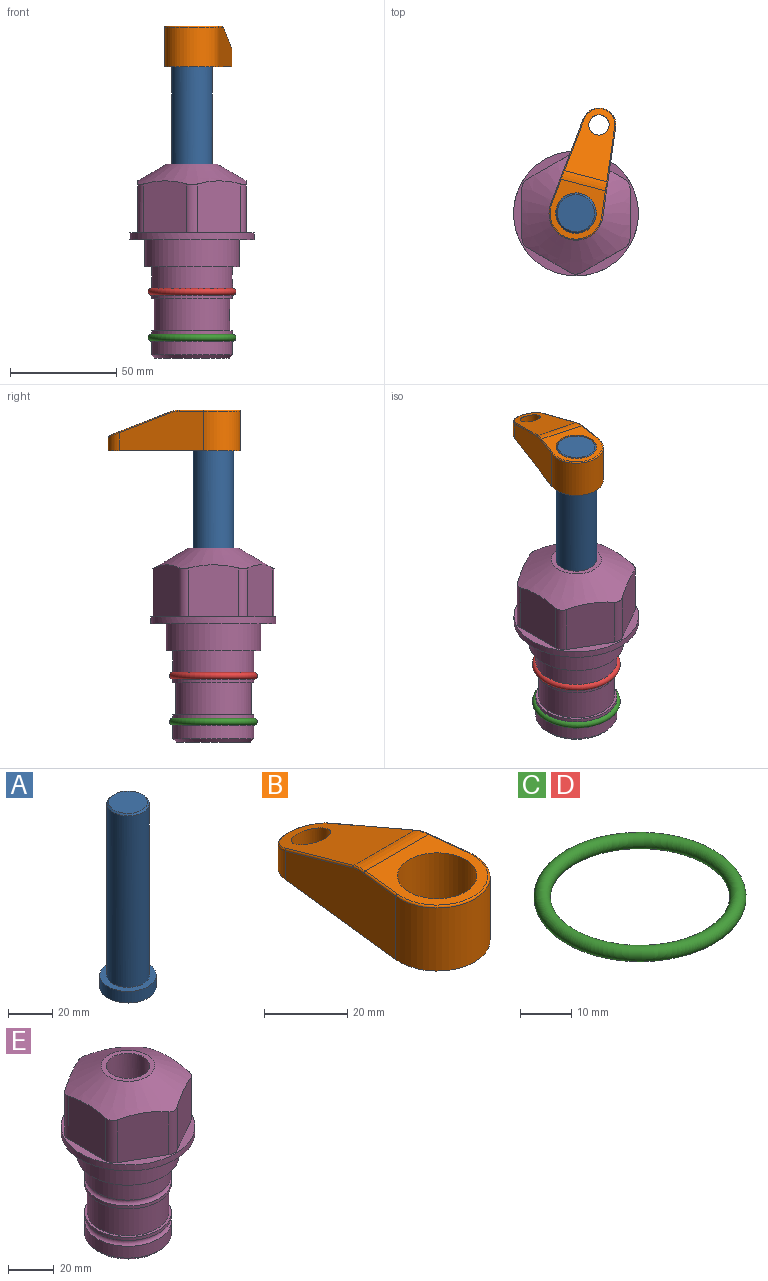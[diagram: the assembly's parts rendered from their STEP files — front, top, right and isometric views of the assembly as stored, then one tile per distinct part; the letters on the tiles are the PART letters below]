
ASSEMBLY  parts=5 mates=3
PART A: 6 faces, bbox 25.4x25.4x101.6 mm
  f0: plane 17.46x17.46mm, normal (0,0,1), area 239.5mm2, adj f5
  f1: plane 25.4x25.4mm, normal (0,0,-1), area 506.7mm2, adj f2
  f2: cylinder r=12.7mm len=25.4mm, axis (0,0,1), area 506.7mm2, adj f1,f3
  f3: plane 25.4x25.4mm, normal (0,0,1), area 221.7mm2, adj f2,f4
  f4: cylinder r=9.53mm len=94.46mm, axis (0,0,1), area 5653mm2, adj f3,f5
  f5: cone r=8.73mm half-angle=45deg, axis (0,0,-1), area 64.4mm2, adj f0,f4
PART B: 44 faces, bbox 27.5x64.5x19.1 mm
  f0: plane 2.3x0.95mm, normal (0,0,-1), area 1mm2, adj f25,f30,f34
  f1: plane 63.5x25.4mm, normal (0,0,-1), area 561.7mm2, adj f2,f3,f4,f5,f6,f7,f19,f20
  f2: cylinder r=12.7mm len=25.4mm, axis (0,0,-1), area 792.2mm2, adj f1,f3,f5,f13
  f3: plane 42.33x18.54mm, normal (0.99,0.11,0), area 647mm2, adj f1,f2,f4,f11,f12,f14
  f4: cylinder r=7.94mm len=15.78mm, axis (0,0,-1), area 158.6mm2, adj f1,f3,f5,f16
  f5: plane 42.33x18.54mm, normal (-0.99,0.11,0), area 647mm2, adj f1,f2,f4,f15,f17,f18
  f6: cylinder r=9.53mm len=19.05mm, axis (0,0,-1), area 1140.1mm2, adj f1,f8
  f7: cylinder r=4.76mm len=10.98mm, axis (0,0,-1), area 276.1mm2, adj f1,f9
  f8: plane 25.83x24.38mm, normal (0,0,1), area 262.2mm2, adj f6,f10,f11,f13,f15
  f9: plane 32.49x20.55mm, normal (0,0.34,0.94), area 489.9mm2, adj f7,f10,f14,f16,f18
  f10: cylinder r=12.7mm len=21.49mm, axis (-1,0,0), area 93.2mm2, adj f8,f9,f12,f17
  f11: cylinder r=0.51mm len=12.34mm, axis (0.11,-0.99,0), area 9.9mm2, adj f3,f8,f12,f13
  f12: bspline ~7.62x1.64mm, area 3.5mm2, adj f3,f10,f11,f14
  f13: torus R=12.19mm, axis (0,0,1), area 33.6mm2, adj f2,f8,f11,f15
  f14: cylinder r=0.51mm len=26.01mm, axis (0.1,-0.93,0.34), area 21.6mm2, adj f3,f9,f12,f16
  f15: cylinder r=0.51mm len=12.34mm, axis (0.11,0.99,0), area 9.9mm2, adj f5,f8,f13,f17
  f16: bspline ~15.78x7.05mm, area 15.7mm2, adj f4,f9,f14,f18
  f17: bspline ~7.62x1.64mm, area 3.5mm2, adj f5,f10,f15,f18
  f18: cylinder r=0.51mm len=26.01mm, axis (0.1,0.93,-0.34), area 21.6mm2, adj f5,f9,f16,f17
  f19: plane 21.6x14.29mm, normal (-0.99,-0.11,0), area 242.6mm2, adj f1,f26,f28,f34,f36,f38
  f20: plane 21.6x14.29mm, normal (0.99,-0.11,0), area 242.6mm2, adj f1,f27,f29,f37,f39,f41
  f21: cylinder r=12.7mm len=14.29mm, axis (0,0,-1), area 173.2mm2, adj f1,f26,f27,f30,f31,f33
  f22: cylinder r=7.94mm len=7.63mm, axis (0,0,-1), area 53.8mm2, adj f1,f28,f29,f42
  f23: plane 2.3x0.95mm, normal (0,0,-1), area 1mm2, adj f25,f33,f37
  f24: plane 17.94x12.32mm, normal (0,-0.34,-0.94), area 191.2mm2, adj f25,f38,f41,f42
  f25: cylinder r=9.53mm len=12.93mm, axis (-1,0,0), area 37.5mm2, adj f0,f23,f24,f31,f36,f39
  f26: cylinder r=1.59mm len=14.29mm, axis (0,0,-1), area 49mm2, adj f1,f19,f21,f32
  f27: cylinder r=1.59mm len=14.29mm, axis (0,0,-1), area 49mm2, adj f1,f20,f21,f35
  f28: cylinder r=1.59mm len=7.28mm, axis (0,0,-1), area 22.1mm2, adj f1,f19,f22,f40
  f29: cylinder r=1.59mm len=7.28mm, axis (0,0,-1), area 22.1mm2, adj f1,f20,f22,f43
  f30: torus R=14.29mm, axis (0,0,1), area 5.8mm2, adj f0,f21,f31,f32
  f31: bspline ~11.06x2.73mm, area 20.8mm2, adj f21,f25,f30,f33
  f32: sphere r=1.59mm, area 5.4mm2, adj f26,f30,f34
  f33: torus R=14.29mm, axis (0,0,1), area 5.8mm2, adj f21,f23,f31,f35
  f34: cylinder r=1.59mm len=1.68mm, axis (-0.11,0.99,0), area 2.4mm2, adj f0,f19,f32,f36
  f35: sphere r=1.59mm, area 5.4mm2, adj f27,f33,f37
  f36: bspline ~5.82x2.33mm, area 7.7mm2, adj f19,f25,f34,f38
  f37: cylinder r=1.59mm len=1.68mm, axis (0.11,0.99,0), area 2.4mm2, adj f20,f23,f35,f39
  f38: cylinder r=1.59mm len=18.33mm, axis (0.1,-0.93,0.34), area 46.7mm2, adj f19,f24,f36,f40
  f39: bspline ~5.82x2.33mm, area 7.7mm2, adj f20,f25,f37,f41
  f40: sphere r=1.59mm, area 3.6mm2, adj f28,f38,f42
  f41: cylinder r=1.59mm len=18.33mm, axis (0.1,0.93,-0.34), area 46.7mm2, adj f20,f24,f39,f43
  f42: bspline ~8.31x1.84mm, area 15.3mm2, adj f22,f24,f40,f43
  f43: sphere r=1.59mm, area 3.6mm2, adj f29,f41,f42
PART C: 1 faces, bbox 44.7x44.7x3.2 mm
  f0: torus R=19.05mm, axis (0,0,1), area 1193.9mm2
PART D: same geometry as C
PART E: 36 faces, bbox 58.7x58.7x91.2 mm
  f0: cylinder r=17.78mm len=35.56mm, axis (0,0,1), area 1670.8mm2, adj f23,f24,f31
  f1: cylinder r=19.05mm len=38.1mm, axis (0,0,1), area 1191.9mm2, adj f26,f27,f30
  f2: plane 58.66x58.66mm, normal (0,0,-1), area 1150.6mm2, adj f3,f28
  f3: cylinder r=29.33mm len=58.66mm, axis (0,0,-1), area 585.1mm2, adj f2,f4
  f4: plane 58.66x58.66mm, normal (0,0,1), area 475.9mm2, adj f3,f5,f6,f7,f8,f9,f10,f11
  f5: plane 24.5x20.32mm, normal (-0.5,0.87,0), area 562.8mm2, adj f4,f15,f16,f17
  f6: plane 24.5x20.32mm, normal (0.5,0.87,0), area 562.8mm2, adj f4,f14,f15,f17
  f7: plane 24.5x23.48mm, normal (1,0,0), area 562.8mm2, adj f4,f13,f14,f17
  f8: plane 24.5x20.32mm, normal (0.5,-0.87,0), area 562.8mm2, adj f4,f12,f13,f17
  f9: plane 24.5x20.32mm, normal (-0.5,-0.87,0), area 562.8mm2, adj f4,f11,f12,f17
  f10: plane 24.5x23.48mm, normal (-1,0,0), area 562.8mm2, adj f4,f11,f16,f17
  f11: cylinder r=5.08mm len=23.01mm, axis (0,0,-1), area 121.2mm2, adj f4,f9,f10,f17
  f12: cylinder r=5.08mm len=23.01mm, axis (0,0,-1), area 121.2mm2, adj f4,f8,f9,f17
  f13: cylinder r=5.08mm len=23.01mm, axis (0,0,-1), area 121.2mm2, adj f4,f7,f8,f17
  f14: cylinder r=5.08mm len=23.01mm, axis (0,0,-1), area 121.2mm2, adj f4,f6,f7,f17
  f15: cylinder r=5.08mm len=23.01mm, axis (0,0,-1), area 121.2mm2, adj f4,f5,f6,f17
  f16: cylinder r=5.08mm len=23.01mm, axis (0,0,-1), area 121.2mm2, adj f4,f5,f10,f17
  f17: cone r=11.73mm half-angle=60deg, axis (0,0,-1), area 2071.8mm2, adj f5,f6,f7,f8,f9,f10,f11,f12
  f18: plane 23.46x23.46mm, normal (0,0,1), area 147.4mm2, adj f17,f35
  f19: plane 34.93x34.93mm, normal (0,0,-1), area 958mm2, adj f29
  f20: cylinder r=19.05mm len=38.1mm, axis (0,0,1), area 760.1mm2, adj f21,f29
  f21: torus R=19.05mm, axis (0,0,1), area 565.3mm2, adj f20,f22
  f22: cylinder r=19.05mm len=38.1mm, axis (0,0,1), area 190mm2, adj f21,f23
  f23: plane 38.1x38.1mm, normal (0,0,1), area 146.9mm2, adj f0,f22
  f24: plane 38.1x38.1mm, normal (0,0,-1), area 146.9mm2, adj f0,f25
  f25: cylinder r=19.05mm len=38.1mm, axis (0,0,1), area 190mm2, adj f24,f26
  f26: torus R=19.05mm, axis (0,0,1), area 565.3mm2, adj f1,f25
  f27: plane 44.45x44.45mm, normal (0,0,-1), area 411.7mm2, adj f1,f28
  f28: cylinder r=22.23mm len=44.45mm, axis (0,0,1), area 1773.5mm2, adj f2,f27
  f29: cone r=19.05mm half-angle=45deg, axis (0,0,1), area 257.5mm2, adj f19,f20
  f30: cylinder r=3.17mm len=6.75mm, axis (-1,0,0), area 128mm2, adj f1,f33
  f31: cylinder r=3.17mm len=6.35mm, axis (-1,0,0), area 102.5mm2, adj f0,f33
  f32: plane 25.4x25.4mm, normal (0,0,1), area 506.7mm2, adj f33
  f33: cylinder r=12.7mm len=66.42mm, axis (0,0,-1), area 5236.2mm2, adj f30,f31,f32,f34
  f34: cone r=9.53mm half-angle=30deg, axis (0,0,-1), area 443.4mm2, adj f33,f35
  f35: cylinder r=9.53mm len=19.05mm, axis (0,0,-1), area 849mm2, adj f18,f34
PLACE A rot(axis=(0,0,1),75.4deg) t=(0,0,26.77)mm
PLACE B rot(axis=(0,0,-1),14.6deg) t=(0,0,81.38)mm
PLACE C t=(0,0,-21.59)mm
PLACE D at identity
PLACE E at identity fixed
MATE fastened C.f0 <-> E.f0  axis (0,0,1) through (0,0,-46.1)mm
MATE cylindrical A.f2 <-> E.f0  axis (0,0,1) through (0,0,52.41)mm
MATE fastened B.f2 <-> A.f2  axis (0,0,1) through (0,0,100.43)mm
